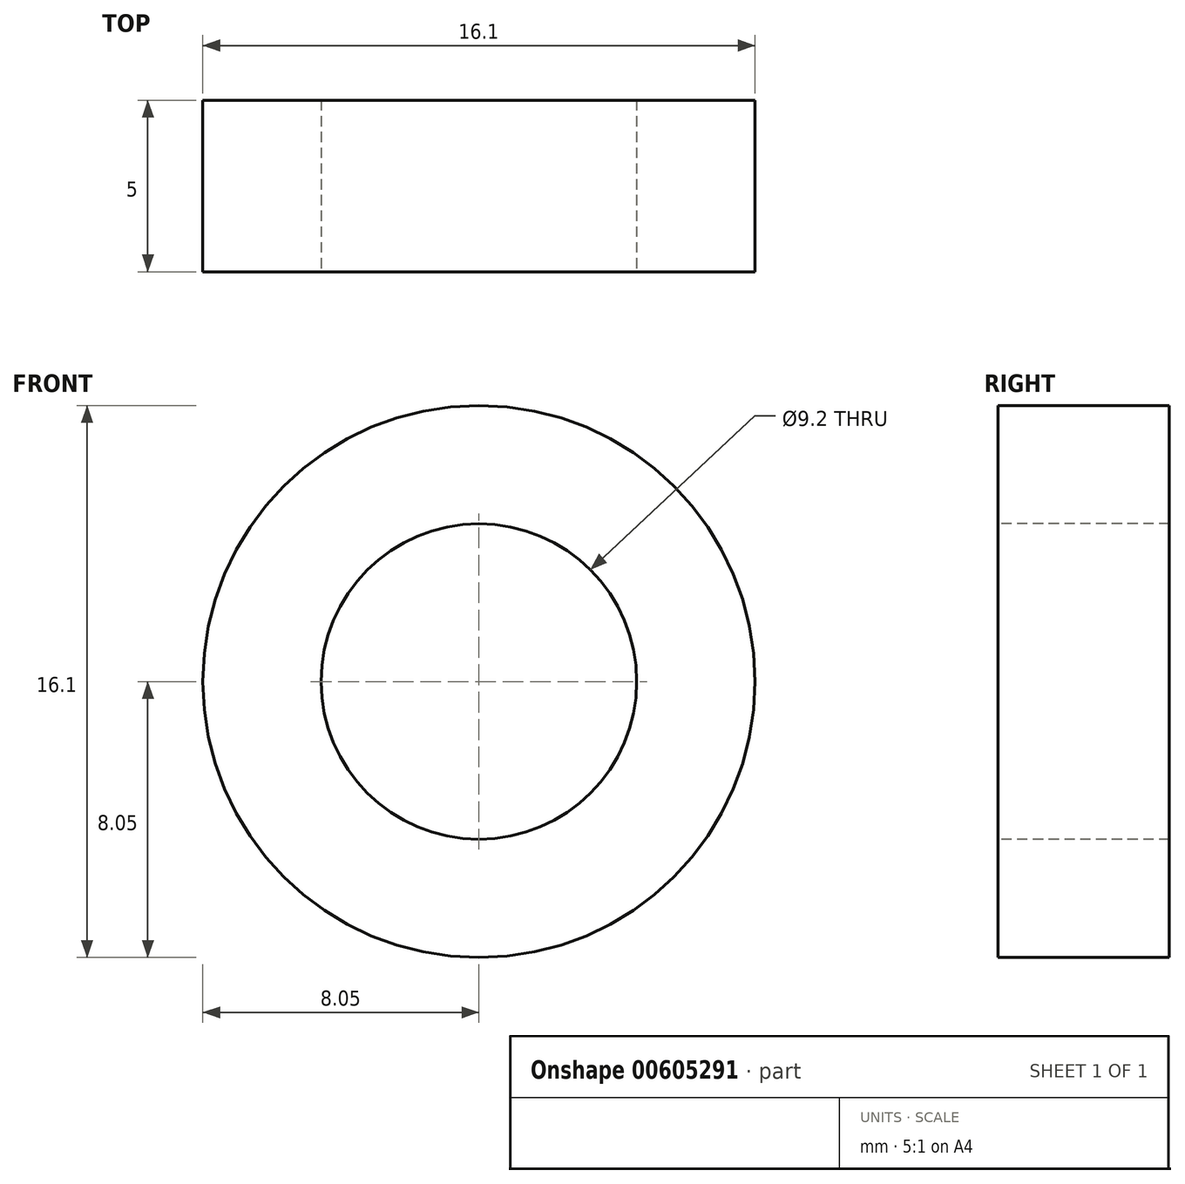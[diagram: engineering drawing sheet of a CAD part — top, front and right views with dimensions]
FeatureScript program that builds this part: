
annotation { "Feature Type Name" : "Feature", "Feature Type Description" : "" }
export const myFeature = defineFeature(function(context is Context, id is Id, definition is map)
    precondition{}
    {
        {
            var Q0;
            Q0=qCreatedBy(makeId("Front.planeOp"),FACE);
            var sketch = newSketch(context, id + "F0", { "sketchPlane" : qUnion([Q0])});
            skCircle(sketch, "E0", {"center": v(0, 0) * mm, "radius": 8.05 * mm});
            skSolve(sketch);
        }
        {
            var Q0;
            Q0 = qSketchRegion(id + "F0", true);
            extrude(context, id + "F1", {"entities" : qUnion([Q0]), "depth" : 5 * mm, "offsetDistance" : 25 * mm});
        }
        {
            var Q0;
            Q0=makeQuery(id+"F1.opExtrude","CAP_FACE",FACE,{"disambiguationData":[OSD([sQuery(id+"F0.wireOp",EDGE,"E0")])],"isStart":false});
            var sketch = newSketch(context, id + "F2", { "sketchPlane" : qUnion([Q0])});
            skCircle(sketch, "E1", {"center": v(0, 0) * mm, "radius": 4.55 * mm});
            skSolve(sketch);
        }
        {
            var Q0;
            Q0=sQuery(id+"F2.wireOp",VERTEX,"E1.center");
            var Q1;
            Q1=makeQuery(id+"F1.opExtrude","SWEPT_BODY",BODY,{"disambiguationData":[OSD([sQuery(id+"F0.wireOp",EDGE,"E0")])]});
            hole(context, id + "F3", {"style" : HoleStyle.SIMPLE, "endStyle" : HoleEndStyle.THROUGH, "holeDiameter" : 9.2 * mm, "majorDiameter" : 5 * mm, "isTappedThrough" : true, "tappedDepth" : 12 * mm, "tapClearance" : 3, "locations" : qUnion([Q0]), "scope" : qUnion([Q1])});
        }
    });
